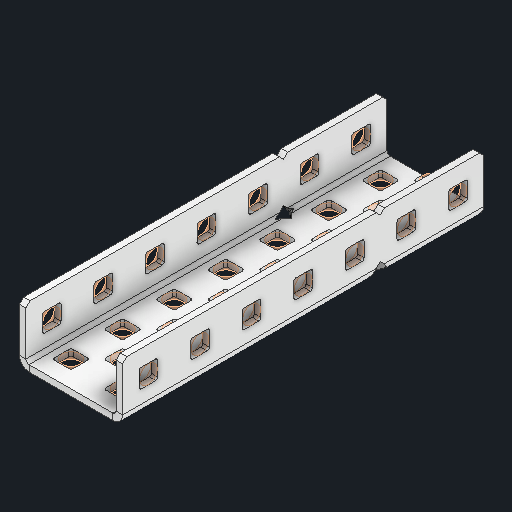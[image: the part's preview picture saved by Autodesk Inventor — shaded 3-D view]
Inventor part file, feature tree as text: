
AUTODESK INVENTOR PART (.ipt)
format: ipt  version: 2024 (Build 280153000, 153)  size: 748,544 bytes
history: native  units: in
note: dims shown in document units (in); Inventor stores cm internally (conversion verified against a paired STEP export)
features: other x42, extrude x33, sheet_metal_op x11, pattern_linear x2, mirror x1, chamfer x1, sketch x1
ambient origin geometry x8: Origin, YZ Plane, XZ Plane, XY Plane, X Axis, Y Axis, Z Axis, Center Point
bodies: Solid1 (feature_tree), Body (feature_tree)
feature tree (91):
  sheet_metal_op  "Flanges"
  other  "Flange Pattern Plane"
  other  "Flange Pattern Sketch"
  sheet_metal_op  "Flange Pattern"
  sheet_metal_op  "Body Pattern"
  pattern_linear  "Center Pattern"  Spacing1=3.5in  [1 undecoded]
  other  "Arc Length"
  mirror  "Notch Mirror"
  pattern_linear  "Notch Pattern"  Spacing1=0.0625in  [1 undecoded]
  chamfer  "End Chamfer"
  extrude  "Half Cut"  Depth=0.0625in
  other  "Plate1"
  sketch  "Sketch2"  dims[d0=1.0in d1=3.5in d2=0.0625in d3=0.0625in d4=0.0312in d5=0.125in d6=0.0625in d7=0.5in d8=90.0deg d9=0.0312in d10=0.25in d11=0.0625in d12=0.0625in d16=0.182in d17=0.02in d18=0.0625in d19=0.0in d20=0.25in d21=0.25in d38=2.7559in d40=0.5in d41=0.7874in d43=1.0in d46=0.172in d47=1.0in d48=0.0in d49=0.182in d50=0.02in d51=0.25in d52=0.25in d53=0.0625in d54=0.0in d55=0.172in d56=1.0in d57=0.0in d58=0.25in d60=2.7559in d62=0.5in d63=0.7874in d65=0.5in d85=0.1473in d86=0.1782in d88=0.04in d89=0.0625in d90=0.0in d91=0.04in d92=0.0491in d95=2.5in d96=0.04in d97=0.25in d98=45.0deg d99=0.25in d100=0.5in d101=0.0in d102=2.497in d106=0.182in d107=0.02in d108=0.5in d109=0.5in d110=0.0625in d111=0.0in d112=0.172in d113=0.5in d114=0.0in d117=0.5in d118=0.5in d119=0.5in]
  other  "Plate2"
  sheet_metal_op  "Bend1"
  sheet_metal_op  "Corner1"
  other  "Srf1"
  other  "Srf2"
  other  "Srf91"
  sheet_metal_op  "Body Pattern Sketch"
  other  "Srf92"
  other  "Srf786"
  other  "Srf823"
  other  "Srf824"
  other  "Srf825"
  other  "Srf826"
  other  "Srf827"
  other  "Srf828"
  other  "Srf829"
  other  "Srf856"
  other  "Srf857"
  other  "Srf858"
  other  "Srf859"
  other  "Srf860"
  other  "Srf861"
  other  "Srf862"
  other  "Srf889"
  other  "Srf890"
  other  "Srf891"
  other  "Srf892"
  other  "Srf893"
  other  "Srf894"
  other  "Srf922"
  other  "Srf923"
  other  "Srf924"
  other  "Srf925"
  other  "Srf926"
  other  "Srf959"
  other  "Srf960"
  other  "Srf961"
  other  "Srf962"
  other  "Srf963"
  sheet_metal_op  "Flange Stamp"
  sheet_metal_op  "Flange Circle"
  sheet_metal_op  "Body Stamp"
  sheet_metal_op  "Body Circle"
  other  "Center Stamp"
  other  "Center Circle"
  sheet_metal_op  "Notch"
  extrude  "ExtrusionSrf2"  Depth=0.0312in
  extrude  "ExtrusionSrf92"  Depth=0.5in
  extrude  "ExtrusionSrf823"  Depth=0.0625in
  extrude  "ExtrusionSrf824"  Depth=0.5in TaperAngle=90.0deg
  extrude  "ExtrusionSrf825"  Depth=0.5in
  extrude  "ExtrusionSrf826"  Depth=0.0625in
  extrude  "ExtrusionSrf827"  Depth=0.0625in
  extrude  "ExtrusionSrf828"  Depth=0.5in
  extrude  "ExtrusionSrf829"  Depth=0.02in
  extrude  "ExtrusionSrf856"  Depth=0.0625in
  extrude  "ExtrusionSrf857"  TaperAngle=0.0deg  [1 undecoded]
  extrude  "ExtrusionSrf858"  Depth=0.5in
  extrude  "ExtrusionSrf859"  Depth=0.5in
  extrude  "ExtrusionSrf860"  Depth=0.5in
  extrude  "ExtrusionSrf861"  Depth=0.5in
  extrude  "ExtrusionSrf862"  Depth=1.0in TaperAngle=0.0deg
  extrude  "ExtrusionSrf889"  Depth=0.5in
  extrude  "ExtrusionSrf890"  Depth=0.02in
  extrude  "ExtrusionSrf891"  Depth=0.5in
  extrude  "ExtrusionSrf892"  Depth=0.5in
  extrude  "ExtrusionSrf893"  Depth=0.0625in
  extrude  "ExtrusionSrf894"  TaperAngle=0.0deg  [1 undecoded]
  extrude  "ExtrusionSrf922"  Depth=0.5in
  extrude  "ExtrusionSrf923"  Depth=1.0in TaperAngle=0.0deg
  extrude  "ExtrusionSrf924"  Depth=0.5in
  extrude  "ExtrusionSrf925"  Depth=0.5in
  extrude  "ExtrusionSrf926"  Depth=0.5in
  extrude  "ExtrusionSrf959"  Depth=0.5in
  extrude  "ExtrusionSrf960"  Depth=0.5in
  extrude  "ExtrusionSrf961"  Depth=0.5in
  extrude  "ExtrusionSrf962"  Depth=0.0625in
  extrude  "ExtrusionSrf963"  TaperAngle=0.0deg  [1 undecoded]
note: 5 required parameter values undecoded (feature->parameter linkage not recoverable at this tier; creation-order binding heuristic only, values carry confidence <= 0.55)
